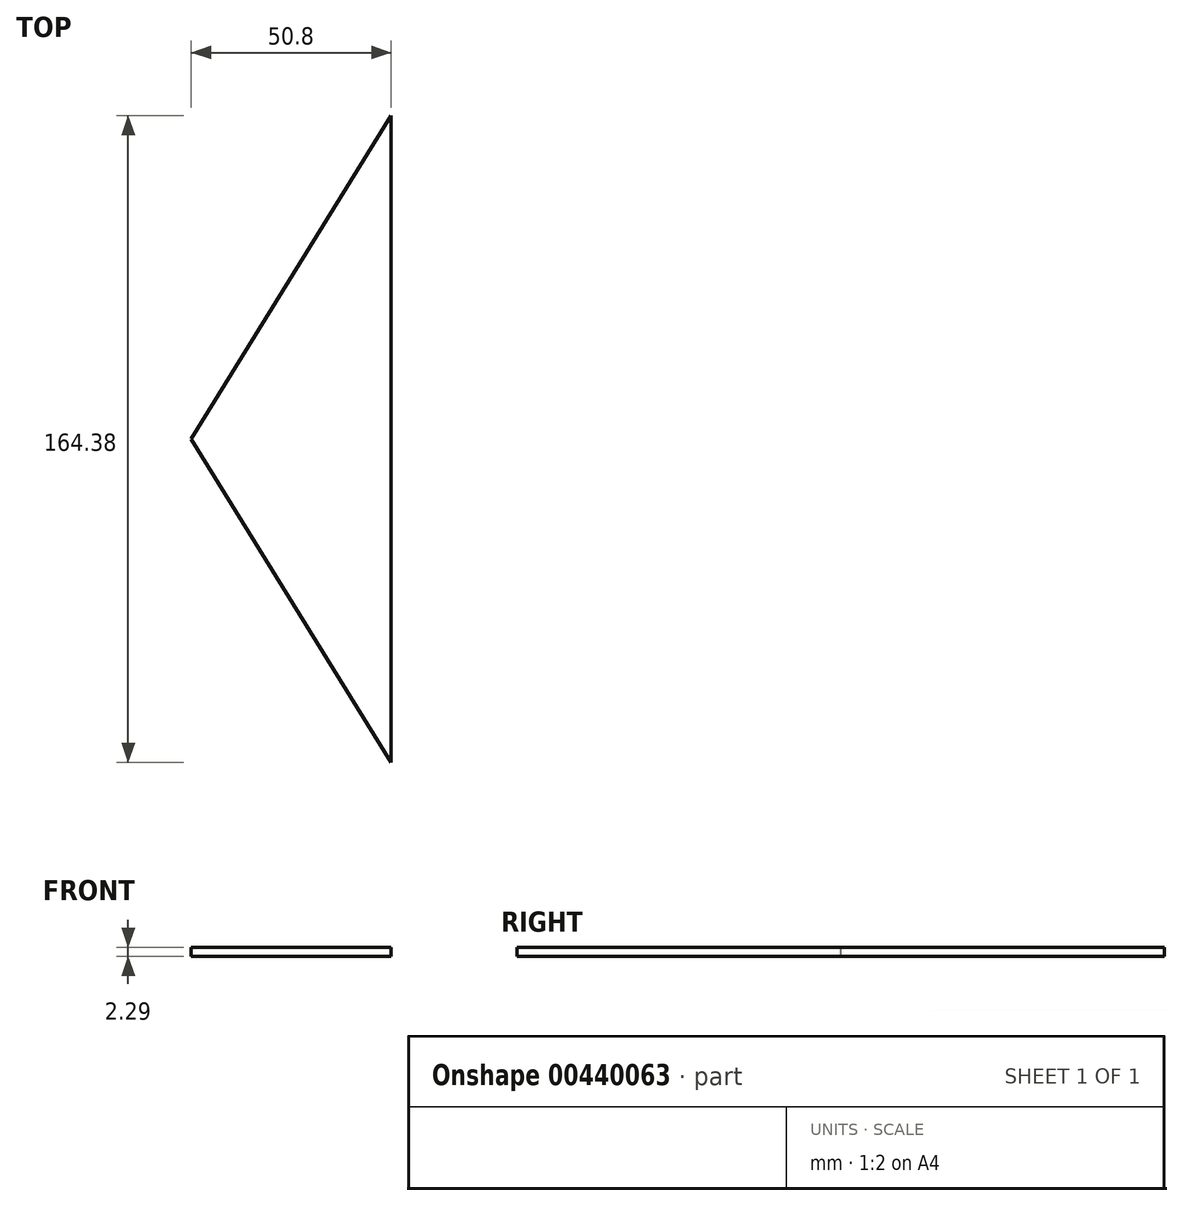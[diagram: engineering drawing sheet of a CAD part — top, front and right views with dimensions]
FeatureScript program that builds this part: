
annotation { "Feature Type Name" : "Feature", "Feature Type Description" : "" }
export const myFeature = defineFeature(function(context is Context, id is Id, definition is map)
    precondition{}
    {
        {
            var Q0;
            Q0=qCreatedBy(makeId("Top.planeOp"),FACE);
            var sketch = newSketch(context, id + "F0", { "sketchPlane" : qUnion([Q0])});
            skLineSegment(sketch, "E0", {"start": v(0, 0) * mm, "end": v(0, 82.2) * mm});
            skLineSegment(sketch, "E1", {"start": v(0, 82.2) * mm, "end": v(-50.8, 0) * mm});
            skLineSegment(sketch, "E2.MirrorCS", {"start": v(0, -82.2) * mm, "end": v(-50.8, 0) * mm});
            skLineSegment(sketch, "E3.MirrorCS", {"start": v(0, 0) * mm, "end": v(0, -82.2) * mm});
            skSolve(sketch);
        }
        {
            var Q0;
            Q0=makeQuery(id+"F0.imprint","IMPRINT",FACE,{"disambiguationData":[TD([[makeQuery(id+"F0.imprint","IMPRINT",EDGE,{"derivedFrom":sQuery(id+"F0.wireOp",EDGE,"E0")}),1.0]])]});
            extrude(context, id + "F1", {"entities" : qUnion([Q0]), "depth" : 2.3 * mm});
        }
    });
